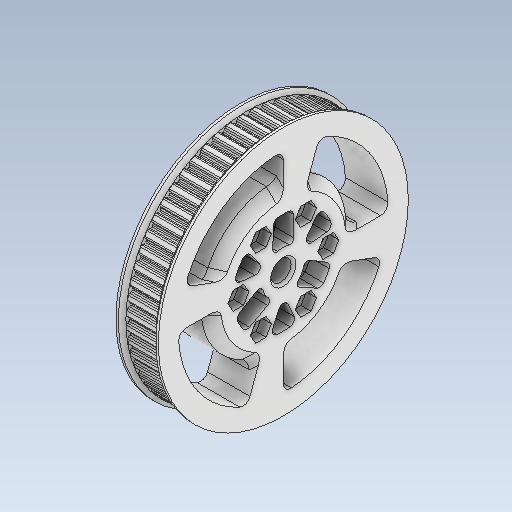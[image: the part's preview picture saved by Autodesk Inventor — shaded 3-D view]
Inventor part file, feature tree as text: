
AUTODESK INVENTOR PART (.ipt)
format: ipt  version: 2020 (Build 240168000, 168)  size: 2,904,576 bytes
history: native  units: mm
features: extrude x13, sketch x13, projected_geometry x8, thicken_offset x7, pattern_circular x7, fillet x7, chamfer x5, other x4, plane x3, reference x1
ambient origin geometry x8: Origin, YZ Plane, XZ Plane, XY Plane, X Axis, Y Axis, Z Axis, Center Point
bodies: Solid1 (feature_tree)
feature tree (68):
  plane  "Work Plane1"
  extrude  "Extrusion1"  Depth=110.0mm
  plane  "Work Plane2"
  extrude  "Extrusion2"  [1 undecoded]
  extrude  "Extrusion3"  Depth=20.0mm TaperAngle=0.0deg
  thicken_offset  "Thicken1"
  extrude  "Extrusion4"  Depth=10.0mm
  extrude  "Extrusion5"  Depth=20.0mm TaperAngle=0.0deg
  extrude  "Extrusion6"  Depth=3.0mm TaperAngle=0.0deg
  thicken_offset  "Thicken9"
  thicken_offset  "Thicken10"
  extrude  "Extrusion20"  Depth=1.0mm
  chamfer  "Chamfer11"  Distance=7.0mm
  chamfer  "Chamfer12"  Distance=2.0mm Angle=45.0deg
  extrude  "Extrusion21"  Depth=2.0mm
  pattern_circular  "Circular Pattern6"  [2 undecoded]
  extrude  "Extrusion22"  Depth=2.0mm
  pattern_circular  "Circular Pattern7"  [2 undecoded]
  fillet  "Fillet10"  Radius=2.0mm
  pattern_circular  "Circular Pattern9"  [2 undecoded]
  fillet  "Fillet11"  Radius=40.0mm
  pattern_circular  "Circular Pattern10"  [2 undecoded]
  extrude  "Extrusion24"  Depth=2.0mm
  fillet  "Fillet12"  Radius=1.5mm
  pattern_circular  "Circular Pattern11"  Count=3  [1 undecoded]
  plane  "Work Plane3"
  extrude  "Extrusion25"  Depth=2.0mm
  extrude  "Extrusion26"  Depth=16.0mm
  thicken_offset  "Thicken14"
  thicken_offset  "Thicken15"
  pattern_circular  "Circular Pattern12"  [2 undecoded]
  chamfer  "Chamfer13"  Distance=13.0mm
  fillet  "Fillet13"  Radius=7.0mm
  fillet  "Fillet14"  Radius=2.0mm
  fillet  "Fillet15"  Radius=4.2mm
  fillet  "Fillet16"  Radius=4.2mm
  chamfer  "Chamfer14"  Distance=30.0mm
  extrude  "Extrusion27"  Depth=2.0mm TaperAngle=0.0deg
  pattern_circular  "Circular Pattern13"  Count=6  [1 undecoded]
  thicken_offset  "Thicken16"
  thicken_offset  "Thicken17"
  chamfer  "Chamfer15"  Distance=88.0mm
  sketch  "Sketch1"  dims[d0=0.0mm d1=110.0mm]
  sketch  "Sketch2"  dims[d2=10.0mm d3=0.0mm d4=-1.0mm]
  sketch  "Sketch3"  dims[d5=110.0mm d6=20.0mm d7=0.0mm]
  projected_geometry  "Projected Loop1"
  sketch  "Sketch4"  dims[d8=20.0mm d9=0.0mm d10=10.0mm d11=9.0mm]
  projected_geometry  "Projected Loop2"
  sketch  "Sketch5"  dims[d12=8.15mm d13=20.0mm d14=0.0mm]
  sketch  "Sketch6"  dims[d15=102.0mm d16=3.0mm d17=0.0mm]
  sketch  "Sketch26"  dims[d18=3.0mm d19=0.0mm d143=1.0mm]
  reference  "Reference6"
  sketch  "Sketch27"  dims[d144=1.0mm]
  projected_geometry  "Projected Loop18"
  sketch  "Sketch28"  dims[d145=1.0mm]
  projected_geometry  "Projected Loop19"
  sketch  "Sketch30"  dims[d146=1.0mm]
  projected_geometry  "Projected Loop21"
  sketch  "Sketch31"  dims[d216=50.0mm d217=7.0mm d218=0.0mm d219=1.5mm d220=2.0mm d221=45.0deg]
  projected_geometry  "Projected Loop22"
  sketch  "Sketch32"  dims[d222=1.5mm d223=2.0mm d224=45.0deg d225=18.0mm]
  projected_geometry  "Projected Loop23"
  projected_geometry  "Projected Loop24"
  sketch  "Sketch33"  dims[d226=4.2mm d227=7.0mm d228=0.0mm d229=60.0mm d230=62.831853mm d232=2.0mm d233=2.0mm d234=17.0mm d235=40.0mm d236=7.0mm d237=0.0mm d238=30.0mm d239=62.831853mm d248=1.5mm d249=30.0mm d250=62.831853mm d252=2.0mm d253=30.0mm d254=62.831853mm d256=16.0mm d257=13.0mm d259=13.0mm d261=7.0mm d262=0.0mm d263=2.0mm d264=4.2mm d265=4.2mm d266=30.0mm d267=62.831853mm d269=3.0mm d270=0.0mm d271=60.0mm d272=88.0mm d273=44.0mm d274=3.5mm d275=3.0mm d276=0.0mm d277=2.0mm d278=2.0mm d279=1.0mm d280=1.0mm d281=40.0mm d282=62.831853mm d284=4.0mm d285=2.0mm d286=45.0deg d287=3.0mm d288=3.0mm d289=3.0mm d290=3.0mm d291=1.0mm d292=2.0mm d293=45.0deg d294=4.2mm d295=60.0mm d297=360.0deg d299=4.0mm d300=0.0mm d301=60.0mm d302=62.831853mm d304=0.5mm d305=0.7mm d306=0.5mm d307=0.7mm d308=1.5mm d309=2.0mm d310=45.0deg]
  other  "_ATP60XL037-A-C12_b"
  parser-record x1  (decoder bookkeeping rows leaked as tree rows — omitted from the tree; the rows remain in map.json)
  other  "joint_base.iam"
  other  "bearing_6810zz:1"
note: 13 required parameter values undecoded (feature->parameter linkage not recoverable at this tier; creation-order binding heuristic only, values carry confidence <= 0.55)
note: 1 file-system path scrubbed to <path> (originals preserved in map.json)
